# Revit family: R20sp
name_source: partatom
category: Pipe Accessories
units: mm (PartAtom-declared; Revit-internal decimal feet)

## family parameters
Always vertical = No
Cut with Voids When Loaded = No
Part Type = Normal
Round Connector Dimension = Use Diameter
Shared = Yes
Work Plane-Based = Yes

## types (3) — shared parameters
Default Elevation = 1219 mm
H2 = 7 mm  [stored 0.0229659 ft]
Manufacturer = Giacomini
R1 = 23 mm

## per-type parameters (varying)
| type | Code | H1 | H4 | H5 | Height | Nut Dimension 1 | Nut dimension 2 | R2 | R3 | Series |
| G 1-1/2”M x R 1-1/2” | R20SPY007 | 21 mm | 63 mm | 15 mm | 40 mm | 61 mm | 49 mm | 24 mm | 25 mm  [stored 0.082021 ft] | R20SP |
| G 2”M x R 2” | R20SPY008 | 21 mm | 67 mm | 16 mm | 41 mm | 82 mm | 62 mm | 30 mm | 31 mm | R20SP |
| G 1-1/4”M x G 1-1/4”M | R20DY016 | 18 mm | 75 mm | 49 mm | 28 mm | 53 mm | 42 mm | 20 mm  [stored 0.0656168 ft] | 21 mm | R20DL |

note: column(s) folded — value = type name in every type: Model

note: [stored X ft] marks values corroborated as IEEE doubles in the binary element streams (Revit-internal decimal feet)

## geometry (parser evidence)
native form markers: Sweep x3
no freeform markers — native parametric forms only
